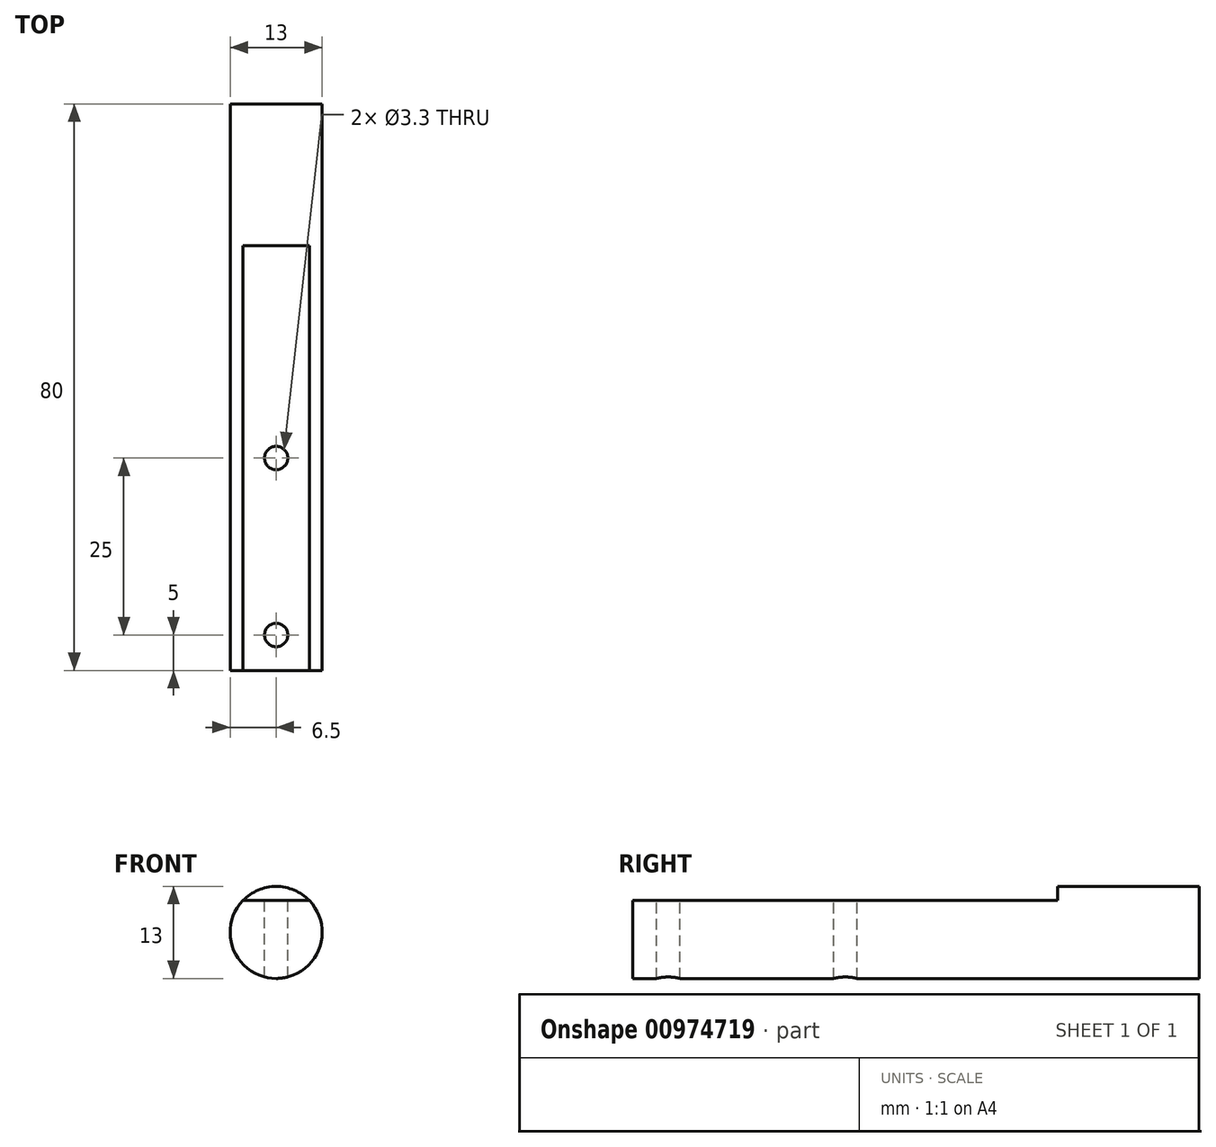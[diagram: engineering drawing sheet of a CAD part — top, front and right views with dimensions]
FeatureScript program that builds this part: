
annotation { "Feature Type Name" : "Feature", "Feature Type Description" : "" }
export const myFeature = defineFeature(function(context is Context, id is Id, definition is map)
    precondition{}
    {
        {
            var Q0;
            Q0=qCreatedBy(makeId("Front.planeOp"),FACE);
            var sketch = newSketch(context, id + "F0", { "sketchPlane" : qUnion([Q0])});
            skPoint(sketch, "E0", {"position": v(0, 0) * mm});
            skCircle(sketch, "E1", {"center": v(0, 0) * mm, "radius": 6.5 * mm});
            skSolve(sketch);
        }
        {
            var Q0;
            Q0 = qSketchRegion(id + "F0", true);
            extrude(context, id + "F1", {"entities" : qUnion([Q0]), "depth" : 80 * mm, "offsetDistance" : 25 * mm});
        }
        {
            var Q0;
            Q0=qCreatedBy(makeId("Top.planeOp"),FACE);
            cPlane(context, id + "F2", {"entities" : qUnion([Q0]), "cplaneType" : CPlaneType.OFFSET, "offset" : 6.5 * mm, "width" : 150 * mm, "height" : 150 * mm});
        }
        {
            var Q0;
            Q0=qCreatedBy(id+"F2.planeOp",FACE);
            var sketch = newSketch(context, id + "F3", { "sketchPlane" : qUnion([Q0])});
            skPoint(sketch, "E2", {"position": v(-17.22, -20) * mm});
            skLineSegment(sketch, "E3.bottom", {"start": v(-17.22, -20) * mm, "end": v(17.18, -20) * mm});
            skLineSegment(sketch, "E3.top", {"start": v(-17.22, -96.47) * mm, "end": v(17.18, -96.47) * mm});
            skLineSegment(sketch, "E3.left", {"start": v(-17.22, -20) * mm, "end": v(-17.22, -96.47) * mm});
            skLineSegment(sketch, "E3.right", {"start": v(17.18, -20) * mm, "end": v(17.18, -96.47) * mm});
            skSolve(sketch);
        }
        {
            var Q0;
            Q0=makeQuery(id+"F3.imprint","IMPRINT",FACE,{"disambiguationData":[TD([[makeQuery(id+"F3.imprint","IMPRINT",EDGE,{"derivedFrom":sQuery(id+"F3.wireOp",EDGE,"E3.bottom")}),-1.0]])]});
            extrude(context, id + "F4", {"entities" : qUnion([Q0]), "operationType" : NewBodyOperationType.REMOVE, "oppositeDirection" : true, "depth" : 2 * mm, "offsetDistance" : 25 * mm});
        }
        {
            var Q0;
            Q0=makeQuery(id+"F4.boolean.opBoolean","COPY",FACE,{"derivedFrom":makeQuery(id+"F4.opExtrude","CAP_FACE",FACE,{"disambiguationData":[OSD([sQuery(id+"F3.wireOp",EDGE,"E3.bottom"),sQuery(id+"F3.wireOp",EDGE,"E3.top"),sQuery(id+"F3.wireOp",EDGE,"E3.left"),sQuery(id+"F3.wireOp",EDGE,"E3.right")])],"isStart":false})});
            var sketch = newSketch(context, id + "F5", { "sketchPlane" : qUnion([Q0])});
            skPoint(sketch, "E4", {"position": v(0, -75) * mm});
            skPoint(sketch, "E4.positionSnap0", {"position": v(0, -80) * mm});
            skPoint(sketch, "E5", {"position": v(0, -50) * mm});
            skSolve(sketch);
        }
        {
            var Q0;
            Q0=sQuery(id+"F5.wireOp",VERTEX,"E5");
            var Q1;
            Q1=sQuery(id+"F5.wireOp",VERTEX,"E4");
            var Q2;
            Q2=makeQuery(id+"F1.opExtrude","SWEPT_BODY",BODY,{"disambiguationData":[OSD([sQuery(id+"F0.wireOp",EDGE,"E1")])]});
            hole(context, id + "F6", {"style" : HoleStyle.SIMPLE, "endStyle" : HoleEndStyle.THROUGH, "standardTappedOrClearance" : lookupTablePath({ "standard" : "ISO", "engagement" : "75%", "pitch" : "0.7 mm", "size" : "M4", "type" : "Tapped" }), "standardBlindInLast" : lookupTablePath({ "standard" : "ISO", "fit" : "Normal", "engagement" : "75%", "pitch" : "0.7 mm", "size" : "M4", "type" : "Clearance & tapped" }), "holeDiameter" : 3.3 * mm, "majorDiameter" : 4 * mm, "showTappedDepth" : true, "isTappedThrough" : true, "tappedDepth" : 12.6 * mm, "tapClearance" : 3, "startFromSketch" : true, "locations" : qUnion([Q0, Q1]), "scope" : qUnion([Q2])});
        }
    });
